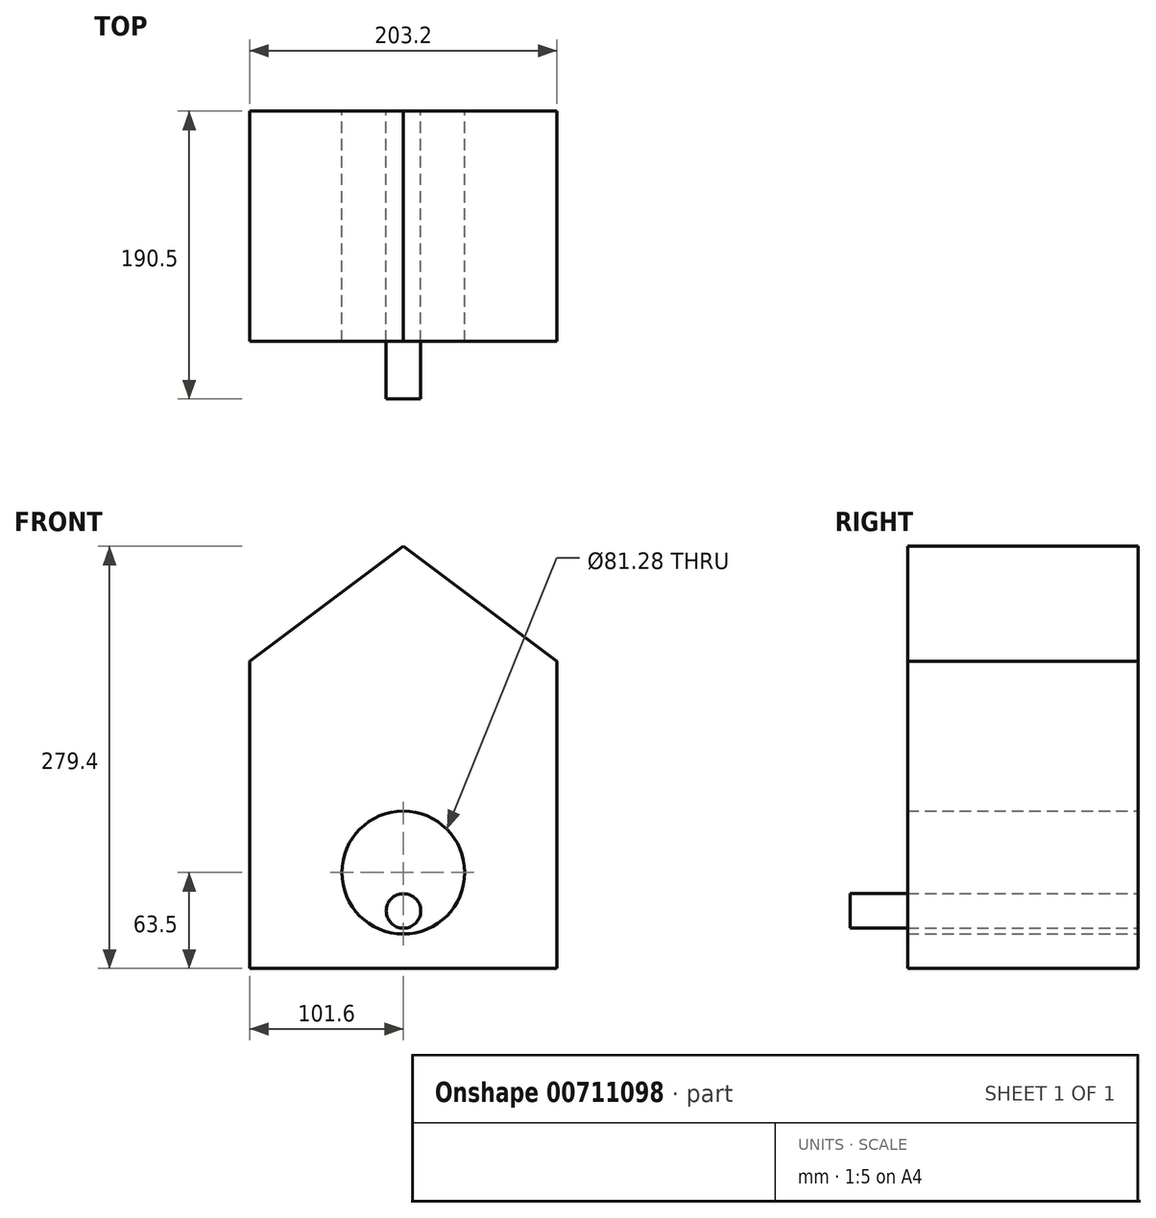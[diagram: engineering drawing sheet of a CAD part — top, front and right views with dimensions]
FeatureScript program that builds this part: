
annotation { "Feature Type Name" : "Feature", "Feature Type Description" : "" }
export const myFeature = defineFeature(function(context is Context, id is Id, definition is map)
    precondition{}
    {
        {
            var Q0;
            Q0=qCreatedBy(makeId("Front.planeOp"),FACE);
            var sketch = newSketch(context, id + "F0", { "sketchPlane" : qUnion([Q0])});
            skLineSegment(sketch, "E0", {"start": v(0, 0) * mm, "end": v(203.2, 0) * mm});
            skLineSegment(sketch, "E1", {"start": v(203.2, 0) * mm, "end": v(203.2, 203.2) * mm});
            skLineSegment(sketch, "E2", {"start": v(0, 0) * mm, "end": v(0, 203.2) * mm});
            skLineSegment(sketch, "E3", {"start": v(0, 203.2) * mm, "end": v(101.6, 279.4) * mm});
            skLineSegment(sketch, "E4", {"start": v(101.6, 279.4) * mm, "end": v(203.2, 203.2) * mm});
            skLineSegment(sketch, "E5", {"start": v(0, 203.2) * mm, "end": v(203.2, 203.2) * mm});
            skCircle(sketch, "E6", {"center": v(101.6, 63.5) * mm, "radius": 40.64 * mm});
            skSolve(sketch);
        }
        {
            var Q0;
            Q0=makeQuery(id+"F0.imprint","IMPRINT",FACE,{"disambiguationData":[TD([[makeQuery(id+"F0.imprint","IMPRINT",EDGE,{"derivedFrom":sQuery(id+"F0.wireOp",EDGE,"E6")}),1.0]])]});
            var sketch = newSketch(context, id + "F1", { "sketchPlane" : qUnion([Q0])});
            skCircle(sketch, "E7", {"center": v(101.7, 38.1) * mm, "radius": 11.43 * mm});
            skSolve(sketch);
        }
        {
            var Q0;
            Q0=makeQuery(id+"F0.imprint","IMPRINT",FACE,{"disambiguationData":[TD([[makeQuery(id+"F0.imprint","IMPRINT",EDGE,{"derivedFrom":sQuery(id+"F0.wireOp",EDGE,"E3")}),-1.0]])]});
            var Q1;
            Q1=makeQuery(id+"F0.imprint","IMPRINT",FACE,{"disambiguationData":[TD([[makeQuery(id+"F0.imprint","IMPRINT",EDGE,{"derivedFrom":sQuery(id+"F0.wireOp",EDGE,"E0")}),1.0]])]});
            extrude(context, id + "F2", {"entities" : qUnion([Q0, Q1]), "depth" : 152.4 * mm, "offsetDistance" : 25.4 * mm});
        }
        {
            var Q0;
            Q0=makeQuery(id+"F1.imprint","IMPRINT",FACE,{"disambiguationData":[TD([[makeQuery(id+"F1.imprint","IMPRINT",EDGE,{"derivedFrom":sQuery(id+"F1.wireOp",EDGE,"E7")}),1.0]])]});
            extrude(context, id + "F3", {"entities" : qUnion([Q0]), "depth" : 190.5 * mm, "offsetDistance" : 25.4 * mm});
        }
    });
